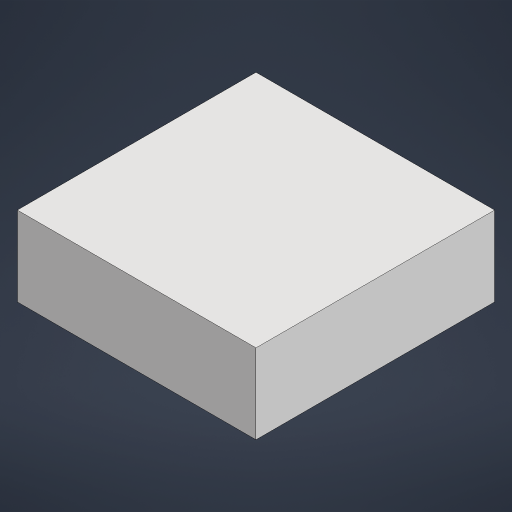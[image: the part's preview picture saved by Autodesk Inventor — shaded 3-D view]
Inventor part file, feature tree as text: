
AUTODESK INVENTOR PART (.ipt)
format: ipt  version: 2023.1 (Build 271208000, 208)  size: 137,728 bytes
history: native  units: in
note: dims shown in document units (in); Inventor stores cm internally (conversion verified against a paired STEP export)
features: extrude x1, sketch x1
ambient origin geometry x8: Origin, YZ Plane, XZ Plane, XY Plane, X Axis, Y Axis, Z Axis, Center Point
bodies: Solid1 (feature_tree)
feature tree (2):
  extrude  "Extrusion1"  Depth=9.0in
  sketch  "Sketch2"  dims[d3=9.0in d4=9.0in d5=3.0in d6=0.0in]
